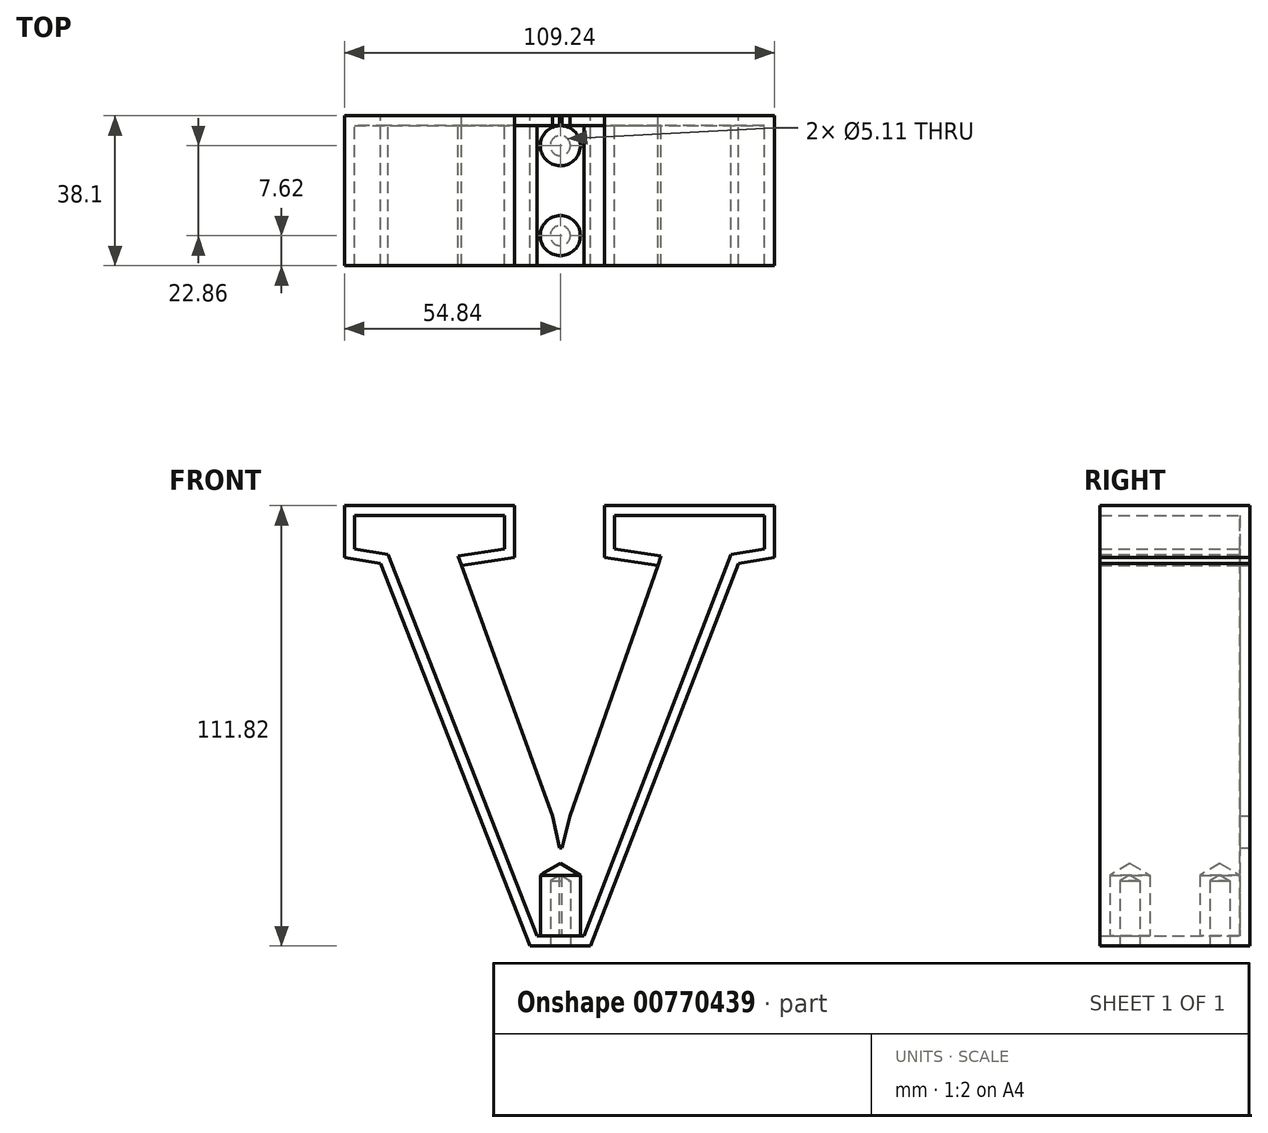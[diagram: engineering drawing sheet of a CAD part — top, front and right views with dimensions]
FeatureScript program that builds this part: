
annotation { "Feature Type Name" : "Feature", "Feature Type Description" : "" }
export const myFeature = defineFeature(function(context is Context, id is Id, definition is map)
    precondition{}
    {
        {
            var Q0;
            Q0=qCreatedBy(makeId("Front.planeOp"),FACE);
            var sketch = newSketch(context, id + "F0", { "sketchPlane" : qUnion([Q0])});
            skText(sketch, "E0", { "text": "v", "fontName": "RobotoSlab-Regular.ttf"});
            const initialGuessF0  = {"E0": [-0.07708, -0.0756, 1, 0, 0.1524]};
            skSetInitialGuess(sketch, initialGuessF0);
            skSolve(sketch);
        }
        {
            var Q0;
            Q0 = qSketchRegion(id + "F0", true);
            extrude(context, id + "F1", {"entities" : qUnion([Q0]), "depth" : 38.1 * mm, "offsetDistance" : 25 * mm});
        }
        {
            var Q0;
            Q0=qCreatedBy(makeId("Top.planeOp"),FACE);
            var sketch = newSketch(context, id + "F2", { "sketchPlane" : qUnion([Q0])});
            skCircle(sketch, "E1", {"center": v(-17.91, -7.62) * mm, "radius": 2.56 * mm});
            skCircle(sketch, "E2", {"center": v(-17.91, -28.48) * mm, "radius": 2.56 * mm});
            skSolve(sketch);
        }
        {
            var Q0;
            Q0=makeQuery(id+"F1.opExtrude","SWEPT_FACE",FACE,{"disambiguationData":[OSD([sQuery(id+"F0.wireOp",EDGE,"E0.sketch_text.stroke-12")])]});
            var sketch = newSketch(context, id + "F3", { "sketchPlane" : qUnion([Q0])});
            skCircle(sketch, "E3", {"center": v(-17.91, 30.48) * mm, "radius": 2.56 * mm});
            skCircle(sketch, "E4", {"center": v(-17.91, 7.62) * mm, "radius": 2.56 * mm});
            skSolve(sketch);
        }
        {
            var Q0;
            Q0=sQuery(id+"F3.wireOp",VERTEX,"E3.center");
            var Q1;
            Q1=sQuery(id+"F3.wireOp",VERTEX,"E4.center");
            var Q2;
            Q2=makeQuery(id+"F1.opExtrude","SWEPT_BODY",BODY,{"disambiguationData":[OSD([sQuery(id+"F0.wireOp",EDGE,"E0.sketch_text.stroke-0"),sQuery(id+"F0.wireOp",EDGE,"E0.sketch_text.stroke-1"),sQuery(id+"F0.wireOp",EDGE,"E0.sketch_text.stroke-2"),sQuery(id+"F0.wireOp",EDGE,"E0.sketch_text.stroke-3"),sQuery(id+"F0.wireOp",EDGE,"E0.sketch_text.stroke-4"),sQuery(id+"F0.wireOp",EDGE,"E0.sketch_text.stroke-5"),sQuery(id+"F0.wireOp",EDGE,"E0.sketch_text.stroke-6"),sQuery(id+"F0.wireOp",EDGE,"E0.sketch_text.stroke-7"),sQuery(id+"F0.wireOp",EDGE,"E0.sketch_text.stroke-8"),sQuery(id+"F0.wireOp",EDGE,"E0.sketch_text.stroke-9"),sQuery(id+"F0.wireOp",EDGE,"E0.sketch_text.stroke-10"),sQuery(id+"F0.wireOp",EDGE,"E0.sketch_text.stroke-11"),sQuery(id+"F0.wireOp",EDGE,"E0.sketch_text.stroke-12"),sQuery(id+"F0.wireOp",EDGE,"E0.sketch_text.stroke-13"),sQuery(id+"F0.wireOp",EDGE,"E0.sketch_text.stroke-14"),sQuery(id+"F0.wireOp",EDGE,"E0.sketch_text.stroke-15"),sQuery(id+"F0.wireOp",EDGE,"E0.sketch_text.stroke-16"),sQuery(id+"F0.wireOp",EDGE,"E0.sketch_text.stroke-17")])]});
            hole(context, id + "F4", {"style" : HoleStyle.SIMPLE, "endStyle" : HoleEndStyle.BLIND, "standardTappedOrClearance" : lookupTablePath({ "standard" : "ANSI", "engagement" : "75%", "pitch" : "20 tpi", "size" : "1/4", "type" : "Tapped" }), "standardBlindInLast" : lookupTablePath({ "standard" : "ANSI", "engagement" : "75%", "pitch" : "20 tpi", "size" : "1/4", "type" : "Tapped" }), "holeDiameter" : 5.1 * mm, "majorDiameter" : 6.35 * mm, "showTappedDepth" : true, "holeDepth" : 16.51 * mm, "tappedDepth" : 12.7 * mm, "tapClearance" : 3, "startFromSketch" : true, "locations" : qUnion([Q0, Q1]), "scope" : qUnion([Q2])});
        }
        {
            var Q0;
            Q0=makeQuery(id+"F1.opExtrude","CAP_FACE",FACE,{"disambiguationData":[OSD([sQuery(id+"F0.wireOp",EDGE,"E0.sketch_text.stroke-0"),sQuery(id+"F0.wireOp",EDGE,"E0.sketch_text.stroke-1"),sQuery(id+"F0.wireOp",EDGE,"E0.sketch_text.stroke-2"),sQuery(id+"F0.wireOp",EDGE,"E0.sketch_text.stroke-3"),sQuery(id+"F0.wireOp",EDGE,"E0.sketch_text.stroke-4"),sQuery(id+"F0.wireOp",EDGE,"E0.sketch_text.stroke-5"),sQuery(id+"F0.wireOp",EDGE,"E0.sketch_text.stroke-6"),sQuery(id+"F0.wireOp",EDGE,"E0.sketch_text.stroke-7"),sQuery(id+"F0.wireOp",EDGE,"E0.sketch_text.stroke-8"),sQuery(id+"F0.wireOp",EDGE,"E0.sketch_text.stroke-9"),sQuery(id+"F0.wireOp",EDGE,"E0.sketch_text.stroke-10"),sQuery(id+"F0.wireOp",EDGE,"E0.sketch_text.stroke-11"),sQuery(id+"F0.wireOp",EDGE,"E0.sketch_text.stroke-12"),sQuery(id+"F0.wireOp",EDGE,"E0.sketch_text.stroke-13"),sQuery(id+"F0.wireOp",EDGE,"E0.sketch_text.stroke-14"),sQuery(id+"F0.wireOp",EDGE,"E0.sketch_text.stroke-15"),sQuery(id+"F0.wireOp",EDGE,"E0.sketch_text.stroke-16"),sQuery(id+"F0.wireOp",EDGE,"E0.sketch_text.stroke-17")])],"isStart":false});
            var Q1;
            Q1=makeQuery(id+"F1.opExtrude","SWEPT_FACE",FACE,{"disambiguationData":[OSD([sQuery(id+"F0.wireOp",EDGE,"E0.sketch_text.stroke-1")])]});
            var Q2;
            Q2=makeQuery(id+"F1.opExtrude","SWEPT_FACE",FACE,{"disambiguationData":[OSD([sQuery(id+"F0.wireOp",EDGE,"E0.sketch_text.stroke-5")])]});
            var Q3;
            Q3=makeQuery(id+"F1.opExtrude","SWEPT_FACE",FACE,{"disambiguationData":[OSD([sQuery(id+"F0.wireOp",EDGE,"E0.sketch_text.stroke-2")])]});
            var Q4;
            Q4=makeQuery(id+"F1.opExtrude","SWEPT_FACE",FACE,{"disambiguationData":[OSD([sQuery(id+"F0.wireOp",EDGE,"E0.sketch_text.stroke-4")])]});
            var Q5;
            Q5=makeQuery(id+"F1.opExtrude","SWEPT_FACE",FACE,{"disambiguationData":[OSD([sQuery(id+"F0.wireOp",EDGE,"E0.sketch_text.stroke-3")])]});
            shell(context, id + "F5", {"entities" : qUnion([Q0, Q1, Q2, Q3, Q4, Q5]), "thickness" : 2.54 * mm});
        }
    });
